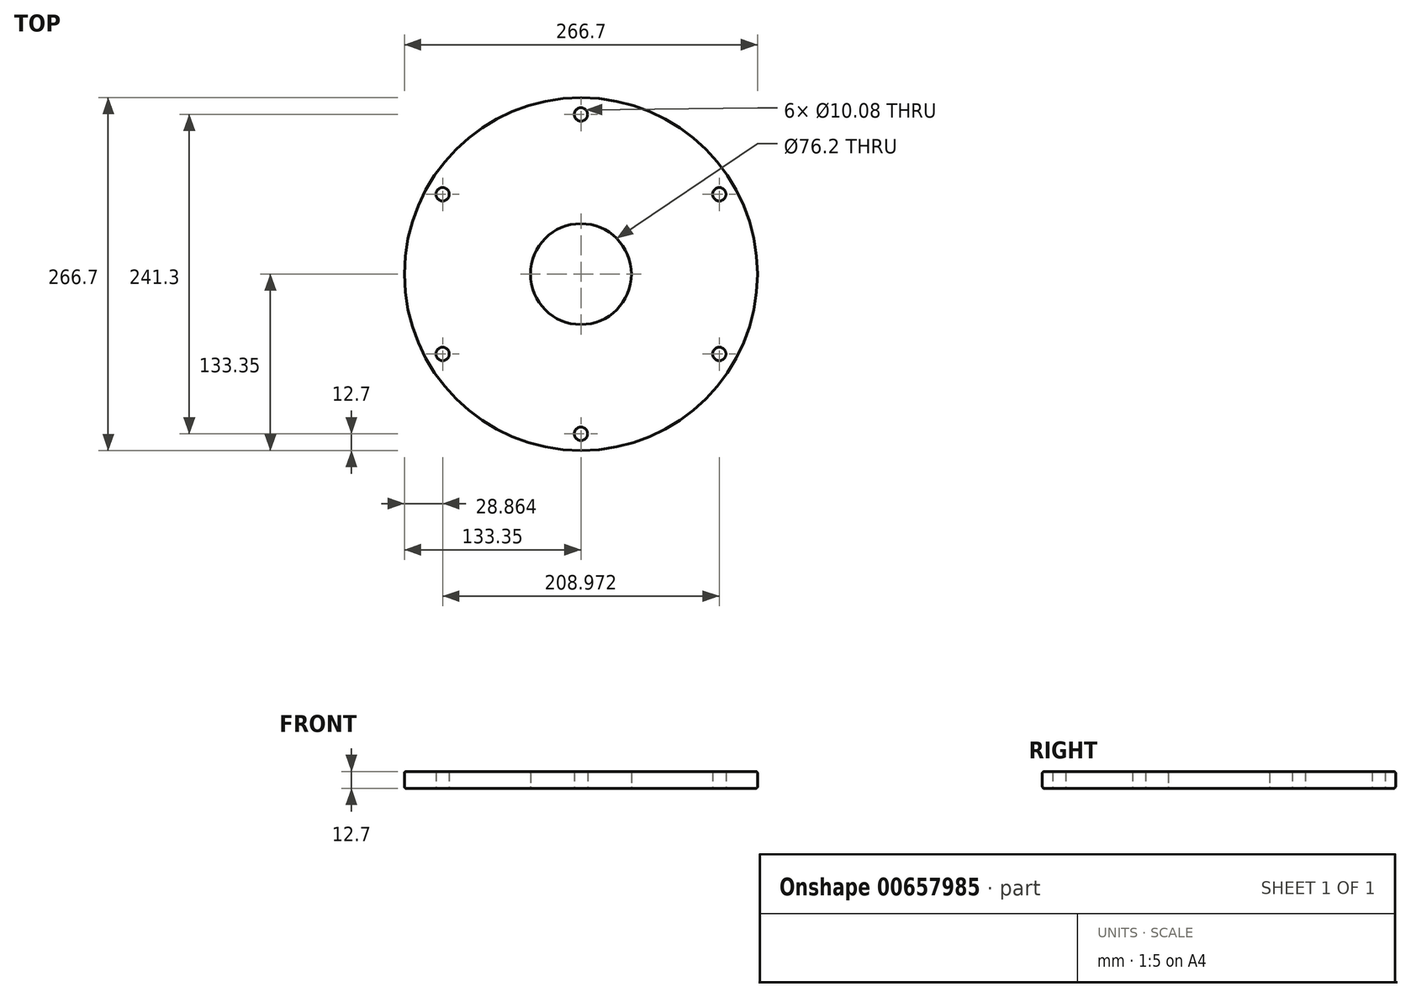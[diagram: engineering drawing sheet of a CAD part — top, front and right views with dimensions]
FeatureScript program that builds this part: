
annotation { "Feature Type Name" : "Feature", "Feature Type Description" : "" }
export const myFeature = defineFeature(function(context is Context, id is Id, definition is map)
    precondition{}
    {
        {
            var Q0;
            Q0=qCreatedBy(makeId("Top.planeOp"),FACE);
            var sketch = newSketch(context, id + "F0", { "sketchPlane" : qUnion([Q0])});
            skCircle(sketch, "E0", {"center": v(0, 0) * mm, "radius": 50.8 * mm, "construction": true});
            skCircle(sketch, "E1", {"center": v(0, 0) * mm, "radius": 101.6 * mm, "construction": true});
            skLineSegment(sketch, "E2", {"start": v(50.8, 0) * mm, "end": v(101.6, 0) * mm, "construction": true});
            skCircle(sketch, "E3", {"center": v(0, 0) * mm, "radius": 133.35 * mm});
            skLineSegment(sketch, "E4.1.0", {"start": v(44, 25.4) * mm, "end": v(87.99, 50.8) * mm, "construction": true});
            skLineSegment(sketch, "E4.2.0", {"start": v(25.4, 44) * mm, "end": v(50.8, 87.99) * mm, "construction": true});
            skLineSegment(sketch, "E4.3.0", {"start": v(0, 50.8) * mm, "end": v(0, 101.6) * mm, "construction": true});
            skLineSegment(sketch, "E4.4.0", {"start": v(-25.4, 44) * mm, "end": v(-50.8, 87.99) * mm, "construction": true});
            skLineSegment(sketch, "E4.5.0", {"start": v(-44, 25.4) * mm, "end": v(-87.99, 50.8) * mm, "construction": true});
            skLineSegment(sketch, "E4.6.0", {"start": v(-50.8, 0) * mm, "end": v(-101.6, 0) * mm, "construction": true});
            skLineSegment(sketch, "E4.7.0", {"start": v(-44, -25.4) * mm, "end": v(-87.99, -50.8) * mm, "construction": true});
            skLineSegment(sketch, "E4.8.0", {"start": v(-25.4, -44) * mm, "end": v(-50.8, -87.99) * mm, "construction": true});
            skLineSegment(sketch, "E4.9.0", {"start": v(0, -50.8) * mm, "end": v(0, -101.6) * mm, "construction": true});
            skLineSegment(sketch, "E4.10.0", {"start": v(25.4, -44) * mm, "end": v(50.8, -87.99) * mm, "construction": true});
            skLineSegment(sketch, "E4.11.0", {"start": v(44, -25.4) * mm, "end": v(87.99, -50.8) * mm, "construction": true});
            skCircle(sketch, "E5", {"center": v(0, 0) * mm, "radius": 38.1 * mm});
            skSolve(sketch);
        }
        {
            var Q0;
            Q0=makeQuery(id+"F0.imprint","IMPRINT",FACE,{"disambiguationData":[TD([[makeQuery(id+"F0.imprint","IMPRINT",EDGE,{"derivedFrom":sQuery(id+"F0.wireOp",EDGE,"E3")}),1.0]])]});
            extrude(context, id + "F1", {"entities" : qUnion([Q0]), "depth" : 12.7 * mm, "offsetDistance" : 25.4 * mm});
        }
        {
            var Q0;
            Q0=makeQuery(id+"F1.opExtrude","CAP_EDGE",EDGE,{"disambiguationData":[OSD([sQuery(id+"F0.wireOp",EDGE,"E5")])],"isStart":false});
            var Q1;
            Q1=makeQuery(id+"F1.opExtrude","CAP_EDGE",EDGE,{"disambiguationData":[OSD([sQuery(id+"F0.wireOp",EDGE,"E5")])],"isStart":true});
            var Q2;
            Q2=makeQuery(id+"F1.opExtrude","CAP_EDGE",EDGE,{"disambiguationData":[OSD([sQuery(id+"F0.wireOp",EDGE,"E3")])],"isStart":false});
            var Q3;
            Q3=makeQuery(id+"F1.opExtrude","CAP_EDGE",EDGE,{"disambiguationData":[OSD([sQuery(id+"F0.wireOp",EDGE,"E3")])],"isStart":true});
            fillet(context, id + "F2", {"entities" : qUnion([Q0, Q1, Q2, Q3]), "radius" : 1.27 * mm, "tangentPropagation" : true, "allowEdgeOverflow" : false});
        }
        {
            var Q0;
            Q0=makeQuery(id+"F1.opExtrude","CAP_FACE",FACE,{"disambiguationData":[OSD([sQuery(id+"F0.wireOp",EDGE,"E3"),sQuery(id+"F0.wireOp",EDGE,"E5")])],"isStart":true});
            var sketch = newSketch(context, id + "F3", { "sketchPlane" : qUnion([Q0])});
            skLineSegment(sketch, "E6", {"start": v(0, 0) * mm, "end": v(0, -120.65) * mm, "construction": true});
            skCircle(sketch, "E7.cCircle", {"center": v(0, 0) * mm, "radius": 120.65 * mm, "construction": true});
            skLineSegment(sketch, "E7.0", {"start": v(0, -120.65) * mm, "end": v(-104.49, -60.33) * mm, "construction": true});
            skLineSegment(sketch, "E7.1", {"start": v(-104.49, -60.33) * mm, "end": v(-104.49, 60.32) * mm, "construction": true});
            skLineSegment(sketch, "E7.2", {"start": v(-104.49, 60.32) * mm, "end": v(0, 120.65) * mm, "construction": true});
            skLineSegment(sketch, "E7.3", {"start": v(0, 120.65) * mm, "end": v(104.49, 60.33) * mm, "construction": true});
            skLineSegment(sketch, "E7.4", {"start": v(104.49, 60.33) * mm, "end": v(104.49, -60.32) * mm, "construction": true});
            skLineSegment(sketch, "E7.5", {"start": v(104.49, -60.32) * mm, "end": v(0, -120.65) * mm, "construction": true});
            skSolve(sketch);
        }
        {
            var Q0;
            Q0=sQuery(id+"F3.wireOp",VERTEX,"E7.5.end");
            var Q1;
            Q1=sQuery(id+"F3.wireOp",VERTEX,"E7.1.start");
            var Q2;
            Q2=sQuery(id+"F3.wireOp",VERTEX,"E7.2.start");
            var Q3;
            Q3=sQuery(id+"F3.wireOp",VERTEX,"E7.3.start");
            var Q4;
            Q4=sQuery(id+"F3.wireOp",VERTEX,"E7.4.start");
            var Q5;
            Q5=sQuery(id+"F3.wireOp",VERTEX,"E7.5.start");
            var Q6;
            Q6=makeQuery(id+"F1.opExtrude","SWEPT_BODY",BODY,{"disambiguationData":[OSD([sQuery(id+"F0.wireOp",EDGE,"E3"),sQuery(id+"F0.wireOp",EDGE,"E5")])]});
            hole(context, id + "F4", {"style" : HoleStyle.SIMPLE, "endStyle" : HoleEndStyle.THROUGH, "standardTappedOrClearance" : lookupTablePath({ "standard" : "ANSI", "fit" : "Normal (ASME)", "size" : "3/8", "type" : "Clearance" }), "standardBlindInLast" : lookupTablePath({ "fit" : "Free", "standard" : "ANSI", "size" : "3/8", "type" : "Clearance" }), "holeDiameter" : 10.08 * mm, "majorDiameter" : 6.35 * mm, "isTappedThrough" : true, "tappedDepth" : 12.7 * mm, "tapClearance" : 3, "locations" : qUnion([Q0, Q1, Q2, Q3, Q4, Q5]), "scope" : qUnion([Q6])});
        }
    });
